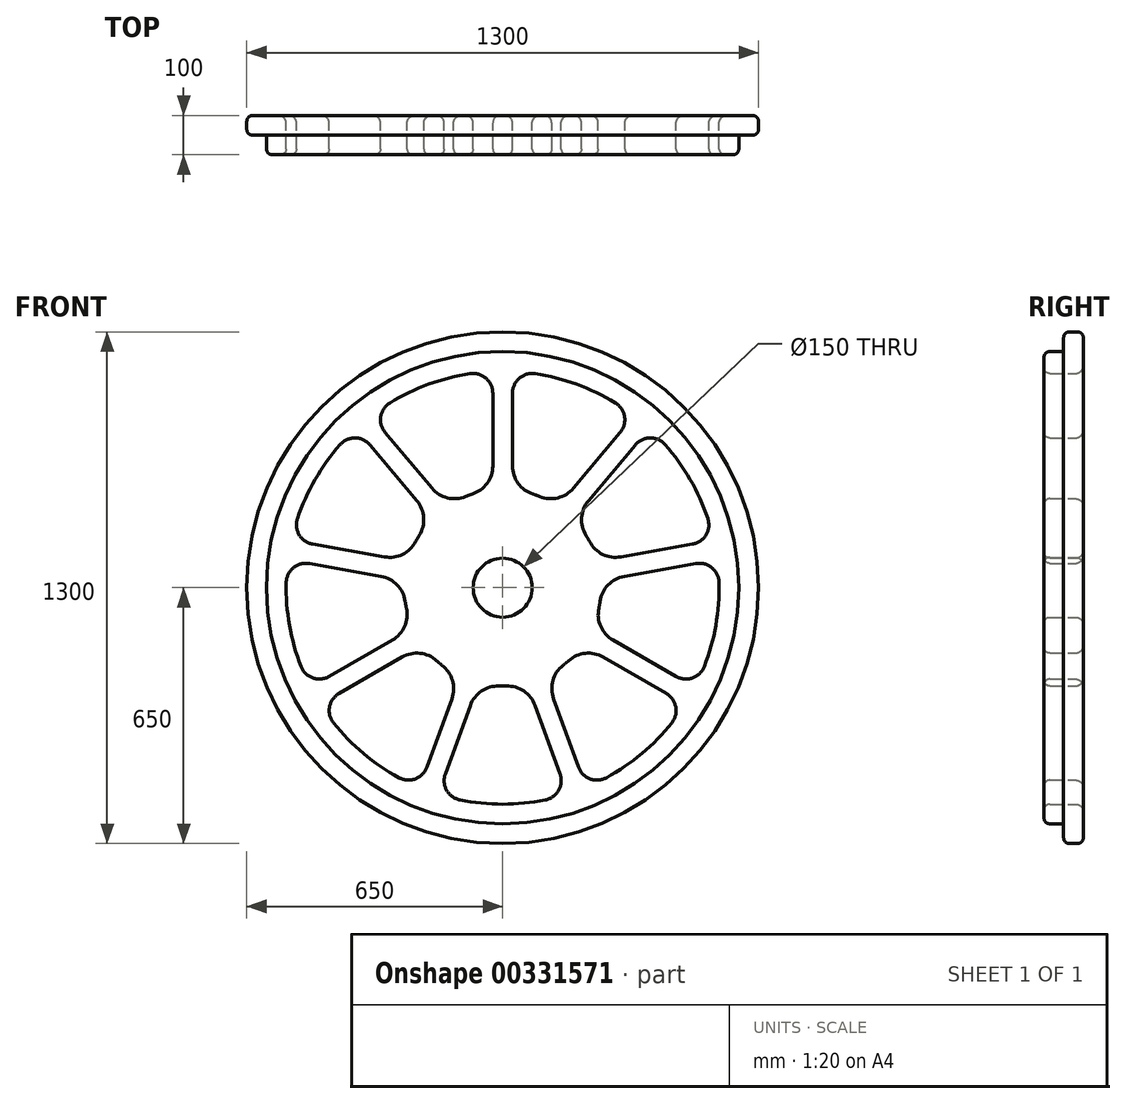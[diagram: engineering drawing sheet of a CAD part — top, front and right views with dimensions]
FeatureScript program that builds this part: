
annotation { "Feature Type Name" : "Feature", "Feature Type Description" : "" }
export const myFeature = defineFeature(function(context is Context, id is Id, definition is map)
    precondition{}
    {
        {
            var Q0;
            Q0=qCreatedBy(makeId("Front.planeOp"),FACE);
            var sketch = newSketch(context, id + "F0", { "sketchPlane" : qUnion([Q0])});
            skCircle(sketch, "E0", {"center": v(0, 0) * mm, "radius": 600 * mm});
            skArc(sketch, "E1", {"start": v(-82.5, 543.78) * mm, "mid": v(-188.11, 516.83) * mm, "end": v(-286.33, 469.59) * mm});
            skArc(sketch, "E2", {"start": v(-211.83, 132.77) * mm, "mid": v(-216.5, 125) * mm, "end": v(-220.9, 117.06) * mm});
            skLineSegment(sketch, "E3", {"start": v(-25, 494.34) * mm, "end": v(-25, 309.23) * mm});
            skLineSegment(sketch, "E4", {"start": v(0, 0) * mm, "end": v(0, 756.87) * mm, "construction": true});
            skLineSegment(sketch, "E5.MirrorCS", {"start": v(25, 494.34) * mm, "end": v(25, 309.23) * mm});
            skLineSegment(sketch, "E6.1.0", {"start": v(-298.6, 394.76) * mm, "end": v(-179.62, 252.96) * mm});
            skLineSegment(sketch, "E6.1.1", {"start": v(-336.9, 362.62) * mm, "end": v(-217.92, 220.82) * mm});
            skLineSegment(sketch, "E6.2.0", {"start": v(-482.5, 110.46) * mm, "end": v(-300.2, 78.32) * mm});
            skLineSegment(sketch, "E6.2.1", {"start": v(-491.17, 61.22) * mm, "end": v(-308.88, 29.08) * mm});
            skLineSegment(sketch, "E6.3.0", {"start": v(-440.61, -225.52) * mm, "end": v(-280.3, -132.97) * mm});
            skLineSegment(sketch, "E6.3.1", {"start": v(-415.61, -268.82) * mm, "end": v(-255.3, -176.27) * mm});
            skLineSegment(sketch, "E6.4.0", {"start": v(-192.57, -455.98) * mm, "end": v(-129.26, -282.03) * mm});
            skLineSegment(sketch, "E6.4.1", {"start": v(-145.58, -473.08) * mm, "end": v(-82.27, -299.13) * mm});
            skLineSegment(sketch, "E6.5.0", {"start": v(145.58, -473.08) * mm, "end": v(82.27, -299.13) * mm});
            skLineSegment(sketch, "E6.5.1", {"start": v(192.57, -455.98) * mm, "end": v(129.26, -282.03) * mm});
            skLineSegment(sketch, "E6.6.0", {"start": v(415.61, -268.82) * mm, "end": v(255.3, -176.27) * mm});
            skLineSegment(sketch, "E6.6.1", {"start": v(440.61, -225.52) * mm, "end": v(280.3, -132.97) * mm});
            skLineSegment(sketch, "E6.7.0", {"start": v(491.17, 61.22) * mm, "end": v(308.88, 29.08) * mm});
            skLineSegment(sketch, "E6.7.1", {"start": v(482.5, 110.46) * mm, "end": v(300.2, 78.32) * mm});
            skLineSegment(sketch, "E6.8.0", {"start": v(336.9, 362.62) * mm, "end": v(217.92, 220.82) * mm});
            skLineSegment(sketch, "E6.8.1", {"start": v(298.6, 394.76) * mm, "end": v(179.62, 252.96) * mm});
            skLineSegment(sketch, "E7", {"start": v(0, 0) * mm, "end": v(502.18, 598.48) * mm, "construction": true});
            skArc(sketch, "E8.trimOffspring", {"start": v(286.33, 469.59) * mm, "mid": v(188.11, 516.83) * mm, "end": v(82.5, 543.78) * mm});
            skPoint(sketch, "E9.visualSharp", {"position": v(334.02, 436.96) * mm});
            skArc(sketch, "E9.filletArc", {"start": v(298.6, 394.76) * mm, "mid": v(309.65, 434.99) * mm, "end": v(286.33, 469.59) * mm});
            skPoint(sketch, "E10.visualSharp", {"position": v(372.32, 404.82) * mm});
            skArc(sketch, "E10.filletArc", {"start": v(412.73, 363.53) * mm, "mid": v(374.61, 380.48) * mm, "end": v(336.9, 362.62) * mm});
            skPoint(sketch, "E11.visualSharp", {"position": v(25, 549.43) * mm});
            skArc(sketch, "E11.filletArc", {"start": v(82.5, 543.78) * mm, "mid": v(42.4, 532.26) * mm, "end": v(25, 494.34) * mm});
            skPoint(sketch, "E12.visualSharp", {"position": v(-25, 549.43) * mm});
            skArc(sketch, "E12.filletArc", {"start": v(-25, 494.34) * mm, "mid": v(-42.4, 532.26) * mm, "end": v(-82.5, 543.78) * mm});
            skArc(sketch, "E13.trimOffspring", {"start": v(-412.73, 363.53) * mm, "mid": v(-476.31, 275) * mm, "end": v(-521.2, 175.67) * mm});
            skArc(sketch, "E14.trimOffspring", {"start": v(-549.84, 13.18) * mm, "mid": v(-541.64, -95.5) * mm, "end": v(-512.17, -200.44) * mm});
            skArc(sketch, "E15.trimOffspring", {"start": v(-429.67, -343.34) * mm, "mid": v(-353.53, -421.32) * mm, "end": v(-263.5, -482.77) * mm});
            skArc(sketch, "E16.trimOffspring", {"start": v(-108.46, -539.2) * mm, "mid": v(0, -550) * mm, "end": v(108.46, -539.2) * mm});
            skArc(sketch, "E17.trimOffspring", {"start": v(263.5, -482.77) * mm, "mid": v(353.53, -421.32) * mm, "end": v(429.67, -343.34) * mm});
            skArc(sketch, "E18.trimOffspring", {"start": v(512.17, -200.44) * mm, "mid": v(541.64, -95.5) * mm, "end": v(549.84, 13.18) * mm});
            skArc(sketch, "E19.trimOffspring", {"start": v(521.2, 175.67) * mm, "mid": v(476.31, 275) * mm, "end": v(412.73, 363.53) * mm});
            skPoint(sketch, "E20.visualSharp", {"position": v(-334.02, 436.96) * mm});
            skArc(sketch, "E20.filletArc", {"start": v(-286.33, 469.59) * mm, "mid": v(-309.65, 434.99) * mm, "end": v(-298.6, 394.76) * mm});
            skPoint(sketch, "E21.visualSharp", {"position": v(-372.32, 404.82) * mm});
            skArc(sketch, "E21.filletArc", {"start": v(-336.9, 362.62) * mm, "mid": v(-374.61, 380.48) * mm, "end": v(-412.73, 363.53) * mm});
            skPoint(sketch, "E22.visualSharp", {"position": v(-536.74, 120.03) * mm});
            skArc(sketch, "E22.filletArc", {"start": v(-521.2, 175.67) * mm, "mid": v(-516.8, 134.19) * mm, "end": v(-482.5, 110.46) * mm});
            skPoint(sketch, "E23.visualSharp", {"position": v(-545.43, 70.79) * mm});
            skArc(sketch, "E23.filletArc", {"start": v(-491.17, 61.22) * mm, "mid": v(-531.53, 50.67) * mm, "end": v(-549.84, 13.18) * mm});
            skPoint(sketch, "E24.visualSharp", {"position": v(-488.32, -253.07) * mm});
            skArc(sketch, "E24.filletArc", {"start": v(-512.17, -200.44) * mm, "mid": v(-482.15, -229.4) * mm, "end": v(-440.61, -225.52) * mm});
            skPoint(sketch, "E25.visualSharp", {"position": v(-463.32, -296.37) * mm});
            skArc(sketch, "E25.filletArc", {"start": v(-415.61, -268.82) * mm, "mid": v(-439.75, -302.85) * mm, "end": v(-429.67, -343.34) * mm});
            skPoint(sketch, "E26.visualSharp", {"position": v(-211.4, -507.75) * mm});
            skArc(sketch, "E26.filletArc", {"start": v(-263.5, -482.77) * mm, "mid": v(-221.89, -485.66) * mm, "end": v(-192.57, -455.98) * mm});
            skPoint(sketch, "E27.visualSharp", {"position": v(-164.42, -524.85) * mm});
            skArc(sketch, "E27.filletArc", {"start": v(-145.58, -473.08) * mm, "mid": v(-142.2, -514.66) * mm, "end": v(-108.46, -539.2) * mm});
            skPoint(sketch, "E28.visualSharp", {"position": v(164.42, -524.85) * mm});
            skArc(sketch, "E28.filletArc", {"start": v(108.46, -539.2) * mm, "mid": v(142.2, -514.66) * mm, "end": v(145.58, -473.08) * mm});
            skPoint(sketch, "E29.visualSharp", {"position": v(211.4, -507.75) * mm});
            skArc(sketch, "E29.filletArc", {"start": v(192.57, -455.98) * mm, "mid": v(221.89, -485.66) * mm, "end": v(263.5, -482.77) * mm});
            skPoint(sketch, "E30.visualSharp", {"position": v(463.32, -296.37) * mm});
            skArc(sketch, "E30.filletArc", {"start": v(429.67, -343.34) * mm, "mid": v(439.75, -302.85) * mm, "end": v(415.61, -268.82) * mm});
            skPoint(sketch, "E31.visualSharp", {"position": v(488.32, -253.07) * mm});
            skArc(sketch, "E31.filletArc", {"start": v(440.61, -225.52) * mm, "mid": v(482.15, -229.4) * mm, "end": v(512.17, -200.44) * mm});
            skPoint(sketch, "E32.visualSharp", {"position": v(545.43, 70.79) * mm});
            skArc(sketch, "E32.filletArc", {"start": v(549.84, 13.18) * mm, "mid": v(531.53, 50.67) * mm, "end": v(491.17, 61.22) * mm});
            skPoint(sketch, "E33.visualSharp", {"position": v(536.74, 120.03) * mm});
            skArc(sketch, "E33.filletArc", {"start": v(482.5, 110.46) * mm, "mid": v(516.8, 134.19) * mm, "end": v(521.2, 175.67) * mm});
            skArc(sketch, "E34.trimOffspring", {"start": v(-76.92, 237.87) * mm, "mid": v(-85.5, 234.92) * mm, "end": v(-93.97, 231.67) * mm});
            skArc(sketch, "E35.trimOffspring", {"start": v(93.97, 231.67) * mm, "mid": v(85.5, 234.92) * mm, "end": v(76.92, 237.87) * mm});
            skArc(sketch, "E36.trimOffspring", {"start": v(220.9, 117.06) * mm, "mid": v(216.5, 125) * mm, "end": v(211.83, 132.77) * mm});
            skArc(sketch, "E37.trimOffspring", {"start": v(244.46, -52.32) * mm, "mid": v(246.2, -43.41) * mm, "end": v(247.62, -34.45) * mm});
            skArc(sketch, "E38.trimOffspring", {"start": v(153.64, -197.22) * mm, "mid": v(160.7, -191.51) * mm, "end": v(167.54, -185.55) * mm});
            skArc(sketch, "E39.trimOffspring", {"start": v(-9.07, -249.84) * mm, "mid": v(0, -250) * mm, "end": v(9.07, -249.84) * mm});
            skArc(sketch, "E40.trimOffspring", {"start": v(-167.54, -185.55) * mm, "mid": v(-160.7, -191.51) * mm, "end": v(-153.64, -197.22) * mm});
            skArc(sketch, "E41.trimOffspring", {"start": v(-247.62, -34.45) * mm, "mid": v(-246.2, -43.41) * mm, "end": v(-244.46, -52.32) * mm});
            skPoint(sketch, "E42.visualSharp", {"position": v(-140.74, 206.62) * mm});
            skArc(sketch, "E42.filletArc", {"start": v(-179.62, 252.96) * mm, "mid": v(-140.26, 228.38) * mm, "end": v(-93.97, 231.67) * mm});
            skPoint(sketch, "E43.newPointA", {"position": v(-25, 248.75) * mm});
            skArc(sketch, "E43.filletArc", {"start": v(-76.92, 237.87) * mm, "mid": v(-39.35, 265.1) * mm, "end": v(-25, 309.23) * mm});
            skPoint(sketch, "E44.visualSharp", {"position": v(25, 248.75) * mm});
            skArc(sketch, "E44.filletArc", {"start": v(25, 309.23) * mm, "mid": v(39.35, 265.1) * mm, "end": v(76.92, 237.87) * mm});
            skPoint(sketch, "E45.newPointB", {"position": v(140.74, 206.62) * mm});
            skArc(sketch, "E45.filletArc", {"start": v(93.97, 231.67) * mm, "mid": v(140.26, 228.38) * mm, "end": v(179.62, 252.96) * mm});
            skPoint(sketch, "E46.visualSharp", {"position": v(179.04, 174.48) * mm});
            skArc(sketch, "E46.filletArc", {"start": v(217.92, 220.82) * mm, "mid": v(200.55, 177.79) * mm, "end": v(211.83, 132.77) * mm});
            skPoint(sketch, "E47.visualSharp", {"position": v(240.63, 67.81) * mm});
            skArc(sketch, "E47.filletArc", {"start": v(220.9, 117.06) * mm, "mid": v(254.25, 84.8) * mm, "end": v(300.2, 78.32) * mm});
            skPoint(sketch, "E48.visualSharp", {"position": v(249.3, 18.57) * mm});
            skArc(sketch, "E48.filletArc", {"start": v(308.88, 29.08) * mm, "mid": v(267.91, 7.28) * mm, "end": v(247.62, -34.45) * mm});
            skPoint(sketch, "E49.visualSharp", {"position": v(227.92, -102.72) * mm});
            skArc(sketch, "E49.filletArc", {"start": v(244.46, -52.32) * mm, "mid": v(249.27, -98.47) * mm, "end": v(280.3, -132.97) * mm});
            skPoint(sketch, "E50.visualSharp", {"position": v(202.92, -146.02) * mm});
            skArc(sketch, "E50.filletArc", {"start": v(255.3, -176.27) * mm, "mid": v(209.91, -166.64) * mm, "end": v(167.54, -185.55) * mm});
            skPoint(sketch, "E51.visualSharp", {"position": v(108.57, -225.2) * mm});
            skArc(sketch, "E51.filletArc", {"start": v(153.64, -197.22) * mm, "mid": v(127.65, -235.66) * mm, "end": v(129.26, -282.03) * mm});
            skPoint(sketch, "E52.visualSharp", {"position": v(61.58, -242.3) * mm});
            skArc(sketch, "E52.filletArc", {"start": v(82.27, -299.13) * mm, "mid": v(53.7, -262.58) * mm, "end": v(9.07, -249.84) * mm});
            skPoint(sketch, "E53.visualSharp", {"position": v(-61.58, -242.3) * mm});
            skArc(sketch, "E53.filletArc", {"start": v(-9.07, -249.84) * mm, "mid": v(-53.7, -262.58) * mm, "end": v(-82.27, -299.13) * mm});
            skPoint(sketch, "E54.visualSharp", {"position": v(-108.57, -225.2) * mm});
            skArc(sketch, "E54.filletArc", {"start": v(-129.26, -282.03) * mm, "mid": v(-127.65, -235.66) * mm, "end": v(-153.64, -197.22) * mm});
            skPoint(sketch, "E55.visualSharp", {"position": v(-202.92, -146.02) * mm});
            skArc(sketch, "E55.filletArc", {"start": v(-167.54, -185.55) * mm, "mid": v(-209.91, -166.64) * mm, "end": v(-255.3, -176.27) * mm});
            skPoint(sketch, "E56.visualSharp", {"position": v(-227.92, -102.72) * mm});
            skArc(sketch, "E56.filletArc", {"start": v(-280.3, -132.97) * mm, "mid": v(-249.27, -98.47) * mm, "end": v(-244.46, -52.32) * mm});
            skPoint(sketch, "E57.visualSharp", {"position": v(-249.3, 18.57) * mm});
            skArc(sketch, "E57.filletArc", {"start": v(-247.62, -34.45) * mm, "mid": v(-267.91, 7.28) * mm, "end": v(-308.88, 29.08) * mm});
            skPoint(sketch, "E58.visualSharp", {"position": v(-240.63, 67.81) * mm});
            skArc(sketch, "E58.filletArc", {"start": v(-300.2, 78.32) * mm, "mid": v(-254.25, 84.8) * mm, "end": v(-220.9, 117.06) * mm});
            skPoint(sketch, "E59.visualSharp", {"position": v(-179.04, 174.48) * mm});
            skArc(sketch, "E59.filletArc", {"start": v(-211.83, 132.77) * mm, "mid": v(-200.55, 177.79) * mm, "end": v(-217.92, 220.82) * mm});
            skCircle(sketch, "E60", {"center": v(0, 0) * mm, "radius": 75 * mm});
            skSolve(sketch);
        }
        {
            var Q0;
            Q0=makeQuery(id+"F0.imprint","IMPRINT",FACE,{"disambiguationData":[TD([[makeQuery(id+"F0.imprint","IMPRINT",EDGE,{"derivedFrom":sQuery(id+"F0.wireOp",EDGE,"E0")}),1.0]])]});
            extrude(context, id + "F1", {"entities" : qUnion([Q0]), "depth" : 100 * mm});
        }
        {
            var Q0;
            Q0=makeQuery(id+"F1.opExtrude","CAP_FACE",FACE,{"disambiguationData":[OSD([sQuery(id+"F0.wireOp",EDGE,"E0"),sQuery(id+"F0.wireOp",EDGE,"E1"),sQuery(id+"F0.wireOp",EDGE,"E2"),sQuery(id+"F0.wireOp",EDGE,"E3"),sQuery(id+"F0.wireOp",EDGE,"E5.MirrorCS"),sQuery(id+"F0.wireOp",EDGE,"E6.1.0"),sQuery(id+"F0.wireOp",EDGE,"E6.1.1"),sQuery(id+"F0.wireOp",EDGE,"E6.2.0"),sQuery(id+"F0.wireOp",EDGE,"E6.2.1"),sQuery(id+"F0.wireOp",EDGE,"E6.3.0"),sQuery(id+"F0.wireOp",EDGE,"E6.3.1"),sQuery(id+"F0.wireOp",EDGE,"E6.4.0"),sQuery(id+"F0.wireOp",EDGE,"E6.4.1"),sQuery(id+"F0.wireOp",EDGE,"E6.5.0"),sQuery(id+"F0.wireOp",EDGE,"E6.5.1"),sQuery(id+"F0.wireOp",EDGE,"E6.6.0"),sQuery(id+"F0.wireOp",EDGE,"E6.6.1"),sQuery(id+"F0.wireOp",EDGE,"E6.7.0"),sQuery(id+"F0.wireOp",EDGE,"E6.7.1"),sQuery(id+"F0.wireOp",EDGE,"E6.8.0"),sQuery(id+"F0.wireOp",EDGE,"E6.8.1"),sQuery(id+"F0.wireOp",EDGE,"E8.trimOffspring"),sQuery(id+"F0.wireOp",EDGE,"E9.filletArc"),sQuery(id+"F0.wireOp",EDGE,"E10.filletArc"),sQuery(id+"F0.wireOp",EDGE,"E11.filletArc"),sQuery(id+"F0.wireOp",EDGE,"E12.filletArc"),sQuery(id+"F0.wireOp",EDGE,"E13.trimOffspring"),sQuery(id+"F0.wireOp",EDGE,"E14.trimOffspring"),sQuery(id+"F0.wireOp",EDGE,"E15.trimOffspring"),sQuery(id+"F0.wireOp",EDGE,"E16.trimOffspring"),sQuery(id+"F0.wireOp",EDGE,"E17.trimOffspring"),sQuery(id+"F0.wireOp",EDGE,"E18.trimOffspring"),sQuery(id+"F0.wireOp",EDGE,"E19.trimOffspring"),sQuery(id+"F0.wireOp",EDGE,"E20.filletArc"),sQuery(id+"F0.wireOp",EDGE,"E21.filletArc"),sQuery(id+"F0.wireOp",EDGE,"E22.filletArc"),sQuery(id+"F0.wireOp",EDGE,"E23.filletArc"),sQuery(id+"F0.wireOp",EDGE,"E24.filletArc"),sQuery(id+"F0.wireOp",EDGE,"E25.filletArc"),sQuery(id+"F0.wireOp",EDGE,"E26.filletArc"),sQuery(id+"F0.wireOp",EDGE,"E27.filletArc"),sQuery(id+"F0.wireOp",EDGE,"E28.filletArc"),sQuery(id+"F0.wireOp",EDGE,"E29.filletArc"),sQuery(id+"F0.wireOp",EDGE,"E30.filletArc"),sQuery(id+"F0.wireOp",EDGE,"E31.filletArc"),sQuery(id+"F0.wireOp",EDGE,"E32.filletArc"),sQuery(id+"F0.wireOp",EDGE,"E33.filletArc"),sQuery(id+"F0.wireOp",EDGE,"E34.trimOffspring"),sQuery(id+"F0.wireOp",EDGE,"E35.trimOffspring"),sQuery(id+"F0.wireOp",EDGE,"E36.trimOffspring"),sQuery(id+"F0.wireOp",EDGE,"E37.trimOffspring"),sQuery(id+"F0.wireOp",EDGE,"E38.trimOffspring"),sQuery(id+"F0.wireOp",EDGE,"E39.trimOffspring"),sQuery(id+"F0.wireOp",EDGE,"E40.trimOffspring"),sQuery(id+"F0.wireOp",EDGE,"E41.trimOffspring"),sQuery(id+"F0.wireOp",EDGE,"E42.filletArc"),sQuery(id+"F0.wireOp",EDGE,"E43.filletArc"),sQuery(id+"F0.wireOp",EDGE,"E44.filletArc"),sQuery(id+"F0.wireOp",EDGE,"E45.filletArc"),sQuery(id+"F0.wireOp",EDGE,"E46.filletArc"),sQuery(id+"F0.wireOp",EDGE,"E47.filletArc"),sQuery(id+"F0.wireOp",EDGE,"E48.filletArc"),sQuery(id+"F0.wireOp",EDGE,"E49.filletArc"),sQuery(id+"F0.wireOp",EDGE,"E50.filletArc"),sQuery(id+"F0.wireOp",EDGE,"E51.filletArc"),sQuery(id+"F0.wireOp",EDGE,"E52.filletArc"),sQuery(id+"F0.wireOp",EDGE,"E53.filletArc"),sQuery(id+"F0.wireOp",EDGE,"E54.filletArc"),sQuery(id+"F0.wireOp",EDGE,"E55.filletArc"),sQuery(id+"F0.wireOp",EDGE,"E56.filletArc"),sQuery(id+"F0.wireOp",EDGE,"E57.filletArc"),sQuery(id+"F0.wireOp",EDGE,"E58.filletArc"),sQuery(id+"F0.wireOp",EDGE,"E59.filletArc"),sQuery(id+"F0.wireOp",EDGE,"E60")])],"isStart":false});
            fillet(context, id + "F2", {"entities" : qUnion([Q0]), "radius" : 15 * mm, "tangentPropagation" : true, "allowEdgeOverflow" : false});
        }
        {
            var Q0;
            Q0=makeQuery(id+"F1.opExtrude","CAP_FACE",FACE,{"disambiguationData":[OSD([sQuery(id+"F0.wireOp",EDGE,"E0"),sQuery(id+"F0.wireOp",EDGE,"E1"),sQuery(id+"F0.wireOp",EDGE,"E2"),sQuery(id+"F0.wireOp",EDGE,"E3"),sQuery(id+"F0.wireOp",EDGE,"E5.MirrorCS"),sQuery(id+"F0.wireOp",EDGE,"E6.1.0"),sQuery(id+"F0.wireOp",EDGE,"E6.1.1"),sQuery(id+"F0.wireOp",EDGE,"E6.2.0"),sQuery(id+"F0.wireOp",EDGE,"E6.2.1"),sQuery(id+"F0.wireOp",EDGE,"E6.3.0"),sQuery(id+"F0.wireOp",EDGE,"E6.3.1"),sQuery(id+"F0.wireOp",EDGE,"E6.4.0"),sQuery(id+"F0.wireOp",EDGE,"E6.4.1"),sQuery(id+"F0.wireOp",EDGE,"E6.5.0"),sQuery(id+"F0.wireOp",EDGE,"E6.5.1"),sQuery(id+"F0.wireOp",EDGE,"E6.6.0"),sQuery(id+"F0.wireOp",EDGE,"E6.6.1"),sQuery(id+"F0.wireOp",EDGE,"E6.7.0"),sQuery(id+"F0.wireOp",EDGE,"E6.7.1"),sQuery(id+"F0.wireOp",EDGE,"E6.8.0"),sQuery(id+"F0.wireOp",EDGE,"E6.8.1"),sQuery(id+"F0.wireOp",EDGE,"E8.trimOffspring"),sQuery(id+"F0.wireOp",EDGE,"E9.filletArc"),sQuery(id+"F0.wireOp",EDGE,"E10.filletArc"),sQuery(id+"F0.wireOp",EDGE,"E11.filletArc"),sQuery(id+"F0.wireOp",EDGE,"E12.filletArc"),sQuery(id+"F0.wireOp",EDGE,"E13.trimOffspring"),sQuery(id+"F0.wireOp",EDGE,"E14.trimOffspring"),sQuery(id+"F0.wireOp",EDGE,"E15.trimOffspring"),sQuery(id+"F0.wireOp",EDGE,"E16.trimOffspring"),sQuery(id+"F0.wireOp",EDGE,"E17.trimOffspring"),sQuery(id+"F0.wireOp",EDGE,"E18.trimOffspring"),sQuery(id+"F0.wireOp",EDGE,"E19.trimOffspring"),sQuery(id+"F0.wireOp",EDGE,"E20.filletArc"),sQuery(id+"F0.wireOp",EDGE,"E21.filletArc"),sQuery(id+"F0.wireOp",EDGE,"E22.filletArc"),sQuery(id+"F0.wireOp",EDGE,"E23.filletArc"),sQuery(id+"F0.wireOp",EDGE,"E24.filletArc"),sQuery(id+"F0.wireOp",EDGE,"E25.filletArc"),sQuery(id+"F0.wireOp",EDGE,"E26.filletArc"),sQuery(id+"F0.wireOp",EDGE,"E27.filletArc"),sQuery(id+"F0.wireOp",EDGE,"E28.filletArc"),sQuery(id+"F0.wireOp",EDGE,"E29.filletArc"),sQuery(id+"F0.wireOp",EDGE,"E30.filletArc"),sQuery(id+"F0.wireOp",EDGE,"E31.filletArc"),sQuery(id+"F0.wireOp",EDGE,"E32.filletArc"),sQuery(id+"F0.wireOp",EDGE,"E33.filletArc"),sQuery(id+"F0.wireOp",EDGE,"E34.trimOffspring"),sQuery(id+"F0.wireOp",EDGE,"E35.trimOffspring"),sQuery(id+"F0.wireOp",EDGE,"E36.trimOffspring"),sQuery(id+"F0.wireOp",EDGE,"E37.trimOffspring"),sQuery(id+"F0.wireOp",EDGE,"E38.trimOffspring"),sQuery(id+"F0.wireOp",EDGE,"E39.trimOffspring"),sQuery(id+"F0.wireOp",EDGE,"E40.trimOffspring"),sQuery(id+"F0.wireOp",EDGE,"E41.trimOffspring"),sQuery(id+"F0.wireOp",EDGE,"E42.filletArc"),sQuery(id+"F0.wireOp",EDGE,"E43.filletArc"),sQuery(id+"F0.wireOp",EDGE,"E44.filletArc"),sQuery(id+"F0.wireOp",EDGE,"E45.filletArc"),sQuery(id+"F0.wireOp",EDGE,"E46.filletArc"),sQuery(id+"F0.wireOp",EDGE,"E47.filletArc"),sQuery(id+"F0.wireOp",EDGE,"E48.filletArc"),sQuery(id+"F0.wireOp",EDGE,"E49.filletArc"),sQuery(id+"F0.wireOp",EDGE,"E50.filletArc"),sQuery(id+"F0.wireOp",EDGE,"E51.filletArc"),sQuery(id+"F0.wireOp",EDGE,"E52.filletArc"),sQuery(id+"F0.wireOp",EDGE,"E53.filletArc"),sQuery(id+"F0.wireOp",EDGE,"E54.filletArc"),sQuery(id+"F0.wireOp",EDGE,"E55.filletArc"),sQuery(id+"F0.wireOp",EDGE,"E56.filletArc"),sQuery(id+"F0.wireOp",EDGE,"E57.filletArc"),sQuery(id+"F0.wireOp",EDGE,"E58.filletArc"),sQuery(id+"F0.wireOp",EDGE,"E59.filletArc"),sQuery(id+"F0.wireOp",EDGE,"E60")])],"isStart":true});
            var sketch = newSketch(context, id + "F3", { "sketchPlane" : qUnion([Q0])});
            skCircle(sketch, "E61", {"center": v(0, 0) * mm, "radius": 600 * mm});
            skCircle(sketch, "E62", {"center": v(0, 0) * mm, "radius": 650 * mm});
            skSolve(sketch);
        }
        {
            var Q0;
            Q0=makeQuery(id+"F3.imprint","IMPRINT",FACE,{"disambiguationData":[TD([[makeQuery(id+"F3.imprint","IMPRINT",EDGE,{"derivedFrom":sQuery(id+"F3.wireOp",EDGE,"E61")}),1.0]])]});
            extrude(context, id + "F4", {"entities" : qUnion([Q0]), "operationType" : NewBodyOperationType.ADD, "oppositeDirection" : true, "depth" : 50 * mm});
        }
        {
            var Q0;
            Q0=makeQuery(id+"F4.opExtrude","CAP_EDGE",EDGE,{"disambiguationData":[OSD([sQuery(id+"F3.wireOp",EDGE,"E62")])],"isStart":false});
            var Q1;
            Q1=makeQuery(id+"F4.opExtrude","CAP_EDGE",EDGE,{"disambiguationData":[OSD([sQuery(id+"F3.wireOp",EDGE,"E61")])],"isStart":false});
            fillet(context, id + "F5", {"entities" : qUnion([Q0, Q1]), "radius" : 14 * mm, "tangentPropagation" : true, "allowEdgeOverflow" : false});
        }
        {
            var Q0;
            Q0=makeQuery(id+"F4.opExtrude","CAP_EDGE",EDGE,{"disambiguationData":[OSD([sQuery(id+"F3.wireOp",EDGE,"E62")])],"isStart":true});
            fillet(context, id + "F6", {"entities" : qUnion([Q0]), "radius" : 15 * mm, "tangentPropagation" : true, "allowEdgeOverflow" : false});
        }
        {
            var Q0;
            Q0=makeQuery(id+"F4.boolean.opBoolean","MERGE",FACE,{"derivedFrom":[makeQuery(id+"F1.opExtrude","CAP_FACE",FACE,{"disambiguationData":[OSD([sQuery(id+"F0.wireOp",EDGE,"E0"),sQuery(id+"F0.wireOp",EDGE,"E1"),sQuery(id+"F0.wireOp",EDGE,"E2"),sQuery(id+"F0.wireOp",EDGE,"E3"),sQuery(id+"F0.wireOp",EDGE,"E5.MirrorCS"),sQuery(id+"F0.wireOp",EDGE,"E6.1.0"),sQuery(id+"F0.wireOp",EDGE,"E6.1.1"),sQuery(id+"F0.wireOp",EDGE,"E6.2.0"),sQuery(id+"F0.wireOp",EDGE,"E6.2.1"),sQuery(id+"F0.wireOp",EDGE,"E6.3.0"),sQuery(id+"F0.wireOp",EDGE,"E6.3.1"),sQuery(id+"F0.wireOp",EDGE,"E6.4.0"),sQuery(id+"F0.wireOp",EDGE,"E6.4.1"),sQuery(id+"F0.wireOp",EDGE,"E6.5.0"),sQuery(id+"F0.wireOp",EDGE,"E6.5.1"),sQuery(id+"F0.wireOp",EDGE,"E6.6.0"),sQuery(id+"F0.wireOp",EDGE,"E6.6.1"),sQuery(id+"F0.wireOp",EDGE,"E6.7.0"),sQuery(id+"F0.wireOp",EDGE,"E6.7.1"),sQuery(id+"F0.wireOp",EDGE,"E6.8.0"),sQuery(id+"F0.wireOp",EDGE,"E6.8.1"),sQuery(id+"F0.wireOp",EDGE,"E8.trimOffspring"),sQuery(id+"F0.wireOp",EDGE,"E9.filletArc"),sQuery(id+"F0.wireOp",EDGE,"E10.filletArc"),sQuery(id+"F0.wireOp",EDGE,"E11.filletArc"),sQuery(id+"F0.wireOp",EDGE,"E12.filletArc"),sQuery(id+"F0.wireOp",EDGE,"E13.trimOffspring"),sQuery(id+"F0.wireOp",EDGE,"E14.trimOffspring"),sQuery(id+"F0.wireOp",EDGE,"E15.trimOffspring"),sQuery(id+"F0.wireOp",EDGE,"E16.trimOffspring"),sQuery(id+"F0.wireOp",EDGE,"E17.trimOffspring"),sQuery(id+"F0.wireOp",EDGE,"E18.trimOffspring"),sQuery(id+"F0.wireOp",EDGE,"E19.trimOffspring"),sQuery(id+"F0.wireOp",EDGE,"E20.filletArc"),sQuery(id+"F0.wireOp",EDGE,"E21.filletArc"),sQuery(id+"F0.wireOp",EDGE,"E22.filletArc"),sQuery(id+"F0.wireOp",EDGE,"E23.filletArc"),sQuery(id+"F0.wireOp",EDGE,"E24.filletArc"),sQuery(id+"F0.wireOp",EDGE,"E25.filletArc"),sQuery(id+"F0.wireOp",EDGE,"E26.filletArc"),sQuery(id+"F0.wireOp",EDGE,"E27.filletArc"),sQuery(id+"F0.wireOp",EDGE,"E28.filletArc"),sQuery(id+"F0.wireOp",EDGE,"E29.filletArc"),sQuery(id+"F0.wireOp",EDGE,"E30.filletArc"),sQuery(id+"F0.wireOp",EDGE,"E31.filletArc"),sQuery(id+"F0.wireOp",EDGE,"E32.filletArc"),sQuery(id+"F0.wireOp",EDGE,"E33.filletArc"),sQuery(id+"F0.wireOp",EDGE,"E34.trimOffspring"),sQuery(id+"F0.wireOp",EDGE,"E35.trimOffspring"),sQuery(id+"F0.wireOp",EDGE,"E36.trimOffspring"),sQuery(id+"F0.wireOp",EDGE,"E37.trimOffspring"),sQuery(id+"F0.wireOp",EDGE,"E38.trimOffspring"),sQuery(id+"F0.wireOp",EDGE,"E39.trimOffspring"),sQuery(id+"F0.wireOp",EDGE,"E40.trimOffspring"),sQuery(id+"F0.wireOp",EDGE,"E41.trimOffspring"),sQuery(id+"F0.wireOp",EDGE,"E42.filletArc"),sQuery(id+"F0.wireOp",EDGE,"E43.filletArc"),sQuery(id+"F0.wireOp",EDGE,"E44.filletArc"),sQuery(id+"F0.wireOp",EDGE,"E45.filletArc"),sQuery(id+"F0.wireOp",EDGE,"E46.filletArc"),sQuery(id+"F0.wireOp",EDGE,"E47.filletArc"),sQuery(id+"F0.wireOp",EDGE,"E48.filletArc"),sQuery(id+"F0.wireOp",EDGE,"E49.filletArc"),sQuery(id+"F0.wireOp",EDGE,"E50.filletArc"),sQuery(id+"F0.wireOp",EDGE,"E51.filletArc"),sQuery(id+"F0.wireOp",EDGE,"E52.filletArc"),sQuery(id+"F0.wireOp",EDGE,"E53.filletArc"),sQuery(id+"F0.wireOp",EDGE,"E54.filletArc"),sQuery(id+"F0.wireOp",EDGE,"E55.filletArc"),sQuery(id+"F0.wireOp",EDGE,"E56.filletArc"),sQuery(id+"F0.wireOp",EDGE,"E57.filletArc"),sQuery(id+"F0.wireOp",EDGE,"E58.filletArc"),sQuery(id+"F0.wireOp",EDGE,"E59.filletArc"),sQuery(id+"F0.wireOp",EDGE,"E60")])],"isStart":true}),makeQuery(id+"F4.opExtrude","CAP_FACE",FACE,{"disambiguationData":[OSD([sQuery(id+"F3.wireOp",EDGE,"E61"),sQuery(id+"F3.wireOp",EDGE,"E62")])],"isStart":true})]});
            fillet(context, id + "F7", {"entities" : qUnion([Q0]), "radius" : 20 * mm, "tangentPropagation" : true, "allowEdgeOverflow" : false});
        }
    });
